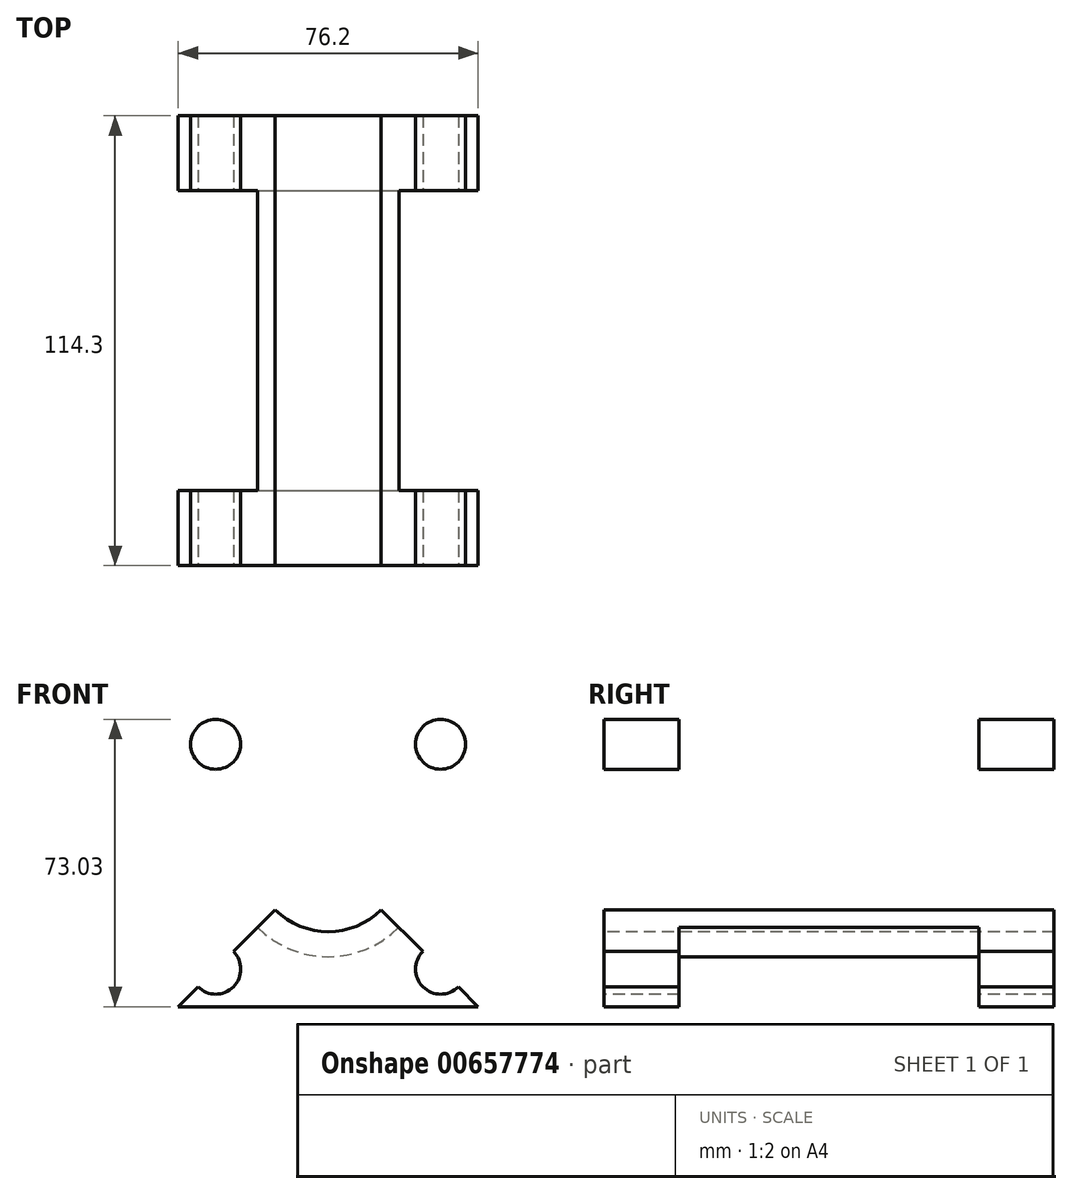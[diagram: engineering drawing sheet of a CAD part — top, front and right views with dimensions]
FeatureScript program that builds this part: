
annotation { "Feature Type Name" : "Feature", "Feature Type Description" : "" }
export const myFeature = defineFeature(function(context is Context, id is Id, definition is map)
    precondition{}
    {
        {
            var Q0;
            Q0=qCreatedBy(makeId("Front.planeOp"),FACE);
            var sketch = newSketch(context, id + "F0", { "sketchPlane" : qUnion([Q0])});
            skLineSegment(sketch, "E0.bottom", {"start": v(-38.1, 38.1) * mm, "end": v(38.1, 38.1) * mm});
            skLineSegment(sketch, "E0.top", {"start": v(-38.1, -38.1) * mm, "end": v(38.1, -38.1) * mm});
            skLineSegment(sketch, "E0.left", {"start": v(-38.1, 38.1) * mm, "end": v(-38.1, -38.1) * mm});
            skLineSegment(sketch, "E0.right", {"start": v(38.1, 38.1) * mm, "end": v(38.1, -38.1) * mm});
            skPoint(sketch, "E0.middle", {"position": v(0, 0) * mm});
            skSolve(sketch);
        }
        {
            var Q0;
            Q0=makeQuery(id+"F0.imprint","IMPRINT",FACE,{"disambiguationData":[TD([[makeQuery(id+"F0.imprint","IMPRINT",EDGE,{"derivedFrom":sQuery(id+"F0.wireOp",EDGE,"E0.bottom")}),-1.0]])]});
            extrude(context, id + "F1", {"entities" : qUnion([Q0]), "depth" : 19.05 * mm, "offsetDistance" : 25.4 * mm});
        }
        {
            var Q0;
            Q0=makeQuery(id+"F1.opExtrude","CAP_FACE",FACE,{"disambiguationData":[OSD([sQuery(id+"F0.wireOp",EDGE,"E0.bottom"),sQuery(id+"F0.wireOp",EDGE,"E0.top"),sQuery(id+"F0.wireOp",EDGE,"E0.left"),sQuery(id+"F0.wireOp",EDGE,"E0.right")])],"isStart":false});
            var sketch = newSketch(context, id + "F2", { "sketchPlane" : qUnion([Q0])});
            skCircle(sketch, "E1", {"center": v(0, 0) * mm, "radius": 25.4 * mm});
            skSolve(sketch);
        }
        {
            var Q0;
            Q0=makeQuery(id+"F2.imprint","IMPRINT",FACE,{"disambiguationData":[TD([[makeQuery(id+"F2.imprint","IMPRINT",EDGE,{"derivedFrom":sQuery(id+"F2.wireOp",EDGE,"E1")}),1.0]])]});
            extrude(context, id + "F3", {"entities" : qUnion([Q0]), "operationType" : NewBodyOperationType.ADD, "depth" : 76.2 * mm, "offsetDistance" : 25.4 * mm});
        }
        {
            var Q0;
            Q0=makeQuery(id+"F3.opExtrude","CAP_FACE",FACE,{"disambiguationData":[OSD([sQuery(id+"F2.wireOp",EDGE,"E1")])],"isStart":false});
            var sketch = newSketch(context, id + "F4", { "sketchPlane" : qUnion([Q0])});
            skLineSegment(sketch, "E2.bottom", {"start": v(-38.1, 38.1) * mm, "end": v(38.1, 38.1) * mm});
            skLineSegment(sketch, "E2.top", {"start": v(-38.1, -38.1) * mm, "end": v(38.1, -38.1) * mm});
            skLineSegment(sketch, "E2.left", {"start": v(-38.1, 38.1) * mm, "end": v(-38.1, -38.1) * mm});
            skLineSegment(sketch, "E2.right", {"start": v(38.1, 38.1) * mm, "end": v(38.1, -38.1) * mm});
            skPoint(sketch, "E2.middle", {"position": v(0, 0) * mm});
            skSolve(sketch);
        }
        {
            var Q0;
            Q0=makeQuery(id+"F4.imprint","IMPRINT",FACE,{"disambiguationData":[TD([[makeQuery(id+"F4.imprint","IMPRINT",EDGE,{"derivedFrom":makeQuery(id+"F3.opExtrude","CAP_EDGE",EDGE,{"disambiguationData":[OSD([sQuery(id+"F2.wireOp",EDGE,"E1")])],"isStart":false})}),1.0]])]});
            var Q1;
            Q1=makeQuery(id+"F4.imprint","IMPRINT",FACE,{"disambiguationData":[TD([[makeQuery(id+"F4.imprint","IMPRINT",EDGE,{"derivedFrom":sQuery(id+"F4.wireOp",EDGE,"E2.bottom")}),-1.0]])]});
            extrude(context, id + "F5", {"entities" : qUnion([Q0, Q1]), "operationType" : NewBodyOperationType.ADD, "depth" : 19.05 * mm, "offsetDistance" : 25.4 * mm});
        }
        {
            var Q0;
            Q0=makeQuery(id+"F5.opExtrude","CAP_FACE",FACE,{"disambiguationData":[OSD([sQuery(id+"F4.wireOp",EDGE,"E2.bottom"),sQuery(id+"F4.wireOp",EDGE,"E2.top"),sQuery(id+"F4.wireOp",EDGE,"E2.left"),sQuery(id+"F4.wireOp",EDGE,"E2.right")])],"isStart":false});
            var sketch = newSketch(context, id + "F6", { "sketchPlane" : qUnion([Q0])});
            skCircle(sketch, "E3", {"center": v(0, 0) * mm, "radius": 19.05 * mm});
            skSolve(sketch);
        }
        {
            var Q0;
            Q0=makeQuery(id+"F6.imprint","IMPRINT",FACE,{"disambiguationData":[TD([[makeQuery(id+"F6.imprint","IMPRINT",EDGE,{"derivedFrom":sQuery(id+"F6.wireOp",EDGE,"E3")}),1.0]])]});
            extrude(context, id + "F7", {"entities" : qUnion([Q0]), "operationType" : NewBodyOperationType.REMOVE, "endBound" : BoundingType.THROUGH_ALL, "oppositeDirection" : true, "depth" : 114.3 * mm, "offsetDistance" : 25.4 * mm});
        }
        {
            var Q0;
            Q0=makeQuery(id+"F5.opExtrude","CAP_FACE",FACE,{"disambiguationData":[OSD([sQuery(id+"F4.wireOp",EDGE,"E2.bottom"),sQuery(id+"F4.wireOp",EDGE,"E2.top"),sQuery(id+"F4.wireOp",EDGE,"E2.left"),sQuery(id+"F4.wireOp",EDGE,"E2.right")])],"isStart":false});
            var sketch = newSketch(context, id + "F8", { "sketchPlane" : qUnion([Q0])});
            skLineSegment(sketch, "E4", {"start": v(-38.1, 38.1) * mm, "end": v(38.1, -38.1) * mm});
            skCircle(sketch, "E5", {"center": v(-28.58, 28.58) * mm, "radius": 6.35 * mm});
            skLineSegment(sketch, "E6", {"start": v(38.1, 38.1) * mm, "end": v(-38.1, -38.1) * mm});
            skCircle(sketch, "E7", {"center": v(-28.58, -28.58) * mm, "radius": 6.35 * mm});
            skCircle(sketch, "E8", {"center": v(28.58, -28.58) * mm, "radius": 6.35 * mm});
            skCircle(sketch, "E9", {"center": v(28.58, 28.58) * mm, "radius": 6.35 * mm});
            skSolve(sketch);
        }
        {
            var Q0;
            {var subQ0=sQuery(id+"F8.wireOp",EDGE,"E5");var subQ1=sQuery(id+"F8.wireOp",EDGE,"E4");var subQ2=makeQuery(id+"F8.imprint","INTERSECT",VERTEX,{"disambiguationData":[OD(0.0)],"derivedFrom":[subQ1,subQ0]});Q0=makeQuery(id+"F8.imprint","IMPRINT",FACE,{"disambiguationData":[TD([[makeQuery(id+"F8.imprint","IMPRINT",EDGE,{"disambiguationData":[TD([[subQ2,-1.0]])],"derivedFrom":subQ1}),-1.0]])]});}
            var Q1;
            {var subQ0=sQuery(id+"F8.wireOp",EDGE,"E5");var subQ1=sQuery(id+"F8.wireOp",EDGE,"E4");var subQ2=makeQuery(id+"F8.imprint","INTERSECT",VERTEX,{"disambiguationData":[OD(0.0)],"derivedFrom":[subQ1,subQ0]});Q1=makeQuery(id+"F8.imprint","IMPRINT",FACE,{"disambiguationData":[TD([[makeQuery(id+"F8.imprint","IMPRINT",EDGE,{"disambiguationData":[TD([[subQ2,-1.0]])],"derivedFrom":subQ1}),1.0]])]});}
            var Q2;
            {var subQ0=sQuery(id+"F8.wireOp",EDGE,"E7");var subQ1=sQuery(id+"F8.wireOp",EDGE,"E6");var subQ2=makeQuery(id+"F8.imprint","INTERSECT",VERTEX,{"disambiguationData":[OD(0.0)],"derivedFrom":[subQ1,subQ0]});Q2=makeQuery(id+"F8.imprint","IMPRINT",FACE,{"disambiguationData":[TD([[makeQuery(id+"F8.imprint","IMPRINT",EDGE,{"disambiguationData":[TD([[subQ2,-1.0]])],"derivedFrom":subQ1}),1.0]])]});}
            var Q3;
            {var subQ0=sQuery(id+"F8.wireOp",EDGE,"E7");var subQ1=sQuery(id+"F8.wireOp",EDGE,"E6");var subQ2=makeQuery(id+"F8.imprint","INTERSECT",VERTEX,{"disambiguationData":[OD(0.0)],"derivedFrom":[subQ1,subQ0]});Q3=makeQuery(id+"F8.imprint","IMPRINT",FACE,{"disambiguationData":[TD([[makeQuery(id+"F8.imprint","IMPRINT",EDGE,{"disambiguationData":[TD([[subQ2,-1.0]])],"derivedFrom":subQ1}),-1.0]])]});}
            var Q4;
            {var subQ0=sQuery(id+"F8.wireOp",EDGE,"E8");var subQ1=sQuery(id+"F8.wireOp",EDGE,"E4");var subQ2=makeQuery(id+"F8.imprint","INTERSECT",VERTEX,{"disambiguationData":[OD(0.0)],"derivedFrom":[subQ1,subQ0]});Q4=makeQuery(id+"F8.imprint","IMPRINT",FACE,{"disambiguationData":[TD([[makeQuery(id+"F8.imprint","IMPRINT",EDGE,{"disambiguationData":[TD([[subQ2,-1.0]])],"derivedFrom":subQ1}),-1.0]])]});}
            var Q5;
            {var subQ0=sQuery(id+"F8.wireOp",EDGE,"E8");var subQ1=sQuery(id+"F8.wireOp",EDGE,"E4");var subQ2=makeQuery(id+"F8.imprint","INTERSECT",VERTEX,{"disambiguationData":[OD(0.0)],"derivedFrom":[subQ1,subQ0]});Q5=makeQuery(id+"F8.imprint","IMPRINT",FACE,{"disambiguationData":[TD([[makeQuery(id+"F8.imprint","IMPRINT",EDGE,{"disambiguationData":[TD([[subQ2,-1.0]])],"derivedFrom":subQ1}),1.0]])]});}
            var Q6;
            {var subQ0=sQuery(id+"F8.wireOp",EDGE,"E9");var subQ1=sQuery(id+"F8.wireOp",EDGE,"E6");var subQ2=makeQuery(id+"F8.imprint","INTERSECT",VERTEX,{"disambiguationData":[OD(0.0)],"derivedFrom":[subQ1,subQ0]});Q6=makeQuery(id+"F8.imprint","IMPRINT",FACE,{"disambiguationData":[TD([[makeQuery(id+"F8.imprint","IMPRINT",EDGE,{"disambiguationData":[TD([[subQ2,-1.0]])],"derivedFrom":subQ1}),1.0]])]});}
            var Q7;
            {var subQ0=sQuery(id+"F8.wireOp",EDGE,"E9");var subQ1=sQuery(id+"F8.wireOp",EDGE,"E6");var subQ2=makeQuery(id+"F8.imprint","INTERSECT",VERTEX,{"disambiguationData":[OD(0.0)],"derivedFrom":[subQ1,subQ0]});Q7=makeQuery(id+"F8.imprint","IMPRINT",FACE,{"disambiguationData":[TD([[makeQuery(id+"F8.imprint","IMPRINT",EDGE,{"disambiguationData":[TD([[subQ2,-1.0]])],"derivedFrom":subQ1}),-1.0]])]});}
            extrude(context, id + "F9", {"entities" : qUnion([Q0, Q1, Q2, Q3, Q4, Q5, Q6, Q7]), "operationType" : NewBodyOperationType.REMOVE, "endBound" : BoundingType.THROUGH_ALL, "oppositeDirection" : true, "depth" : 25.4 * mm, "offsetDistance" : 25.4 * mm});
        }
    });
